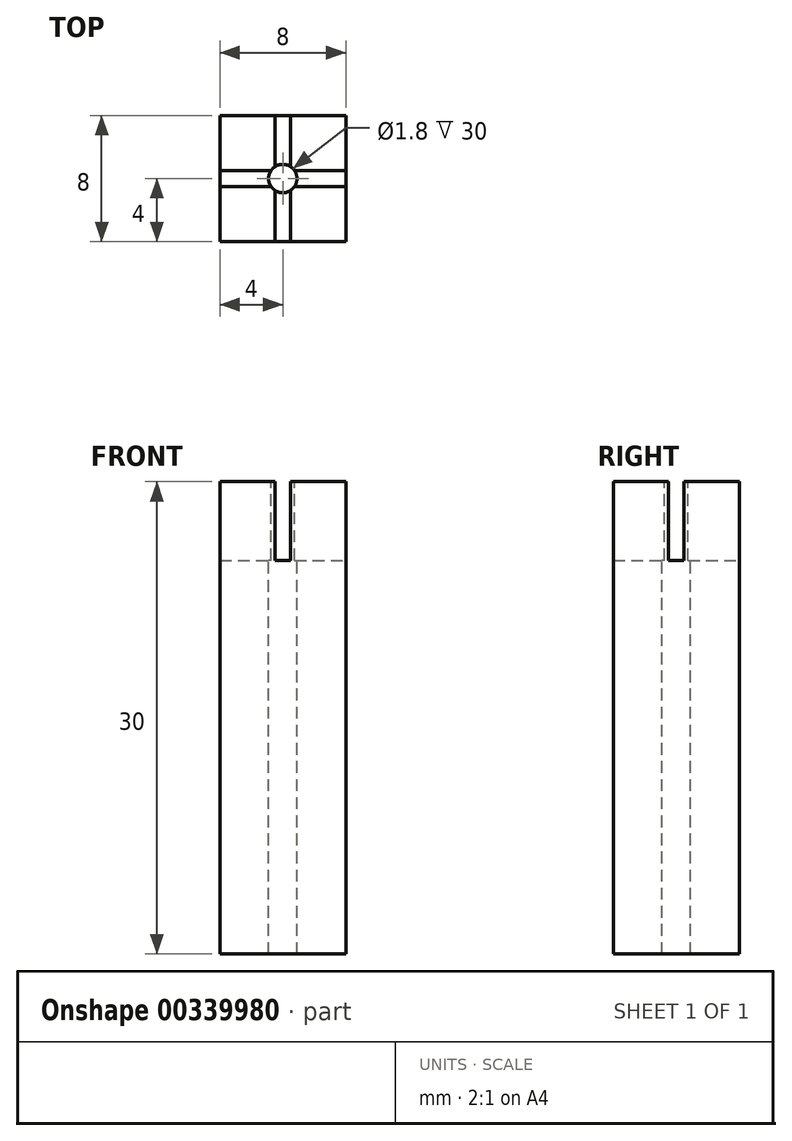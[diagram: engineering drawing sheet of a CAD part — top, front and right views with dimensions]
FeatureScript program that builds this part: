
annotation { "Feature Type Name" : "Feature", "Feature Type Description" : "" }
export const myFeature = defineFeature(function(context is Context, id is Id, definition is map)
    precondition{}
    {
        {
            var Q0;
            Q0=qCreatedBy(makeId("Top.planeOp"),FACE);
            var sketch = newSketch(context, id + "F0", { "sketchPlane" : qUnion([Q0])});
            skLineSegment(sketch, "E0.bottom", {"start": v(4, -4) * mm, "end": v(-4, -4) * mm});
            skLineSegment(sketch, "E0.top", {"start": v(4, 4) * mm, "end": v(-4, 4) * mm});
            skLineSegment(sketch, "E0.left", {"start": v(4, -4) * mm, "end": v(4, 4) * mm});
            skLineSegment(sketch, "E0.right", {"start": v(-4, -4) * mm, "end": v(-4, 4) * mm});
            skPoint(sketch, "E0.middle", {"position": v(0, 0) * mm});
            skSolve(sketch);
        }
        {
            var Q0;
            Q0 = qSketchRegion(id + "F0", true);
            extrude(context, id + "F1", {"entities" : qUnion([Q0]), "depth" : 15 * mm, "hasSecondDirection" : true, "secondDirectionOppositeDirection" : true, "secondDirectionDepth" : 15 * mm});
        }
        {
            var Q0;
            Q0=makeQuery(id+"F1.opExtrude","CAP_FACE",FACE,{"disambiguationData":[OSD([sQuery(id+"F0.wireOp",EDGE,"E0.bottom"),sQuery(id+"F0.wireOp",EDGE,"E0.top"),sQuery(id+"F0.wireOp",EDGE,"E0.left"),sQuery(id+"F0.wireOp",EDGE,"E0.right")])],"isStart":false});
            var sketch = newSketch(context, id + "F2", { "sketchPlane" : qUnion([Q0])});
            skCircle(sketch, "E1", {"center": v(0, 0) * mm, "radius": 0.9 * mm});
            skSolve(sketch);
        }
        {
            var Q0;
            Q0 = qSketchRegion(id + "F2", true);
            extrude(context, id + "F3", {"entities" : qUnion([Q0]), "operationType" : NewBodyOperationType.REMOVE, "oppositeDirection" : true, "depth" : 36.9 * mm});
        }
        {
            var Q0;
            Q0=makeQuery(id+"F1.opExtrude","CAP_FACE",FACE,{"disambiguationData":[OSD([sQuery(id+"F0.wireOp",EDGE,"E0.bottom"),sQuery(id+"F0.wireOp",EDGE,"E0.top"),sQuery(id+"F0.wireOp",EDGE,"E0.left"),sQuery(id+"F0.wireOp",EDGE,"E0.right")])],"isStart":false});
            var sketch = newSketch(context, id + "F4", { "sketchPlane" : qUnion([Q0])});
            skLineSegment(sketch, "E2.bottom", {"start": v(-5, -0.5) * mm, "end": v(5, -0.5) * mm});
            skLineSegment(sketch, "E2.top", {"start": v(-5, 0.5) * mm, "end": v(5, 0.5) * mm});
            skLineSegment(sketch, "E2.left", {"start": v(-5, -0.5) * mm, "end": v(-5, 0.5) * mm});
            skLineSegment(sketch, "E2.right", {"start": v(5, -0.5) * mm, "end": v(5, 0.5) * mm});
            skPoint(sketch, "E2.middle", {"position": v(0, 0) * mm});
            skLineSegment(sketch, "E3.bottom", {"start": v(-0.5, -5) * mm, "end": v(0.5, -5) * mm});
            skLineSegment(sketch, "E3.top", {"start": v(-0.5, 5) * mm, "end": v(0.5, 5) * mm});
            skLineSegment(sketch, "E3.left", {"start": v(-0.5, -5) * mm, "end": v(-0.5, 5) * mm});
            skLineSegment(sketch, "E3.right", {"start": v(0.5, -5) * mm, "end": v(0.5, 5) * mm});
            skSolve(sketch);
        }
        {
            var Q0;
            Q0 = qSketchRegion(id + "F4", true);
            extrude(context, id + "F5", {"entities" : qUnion([Q0]), "operationType" : NewBodyOperationType.REMOVE, "oppositeDirection" : true, "depth" : 5 * mm});
        }
    });
